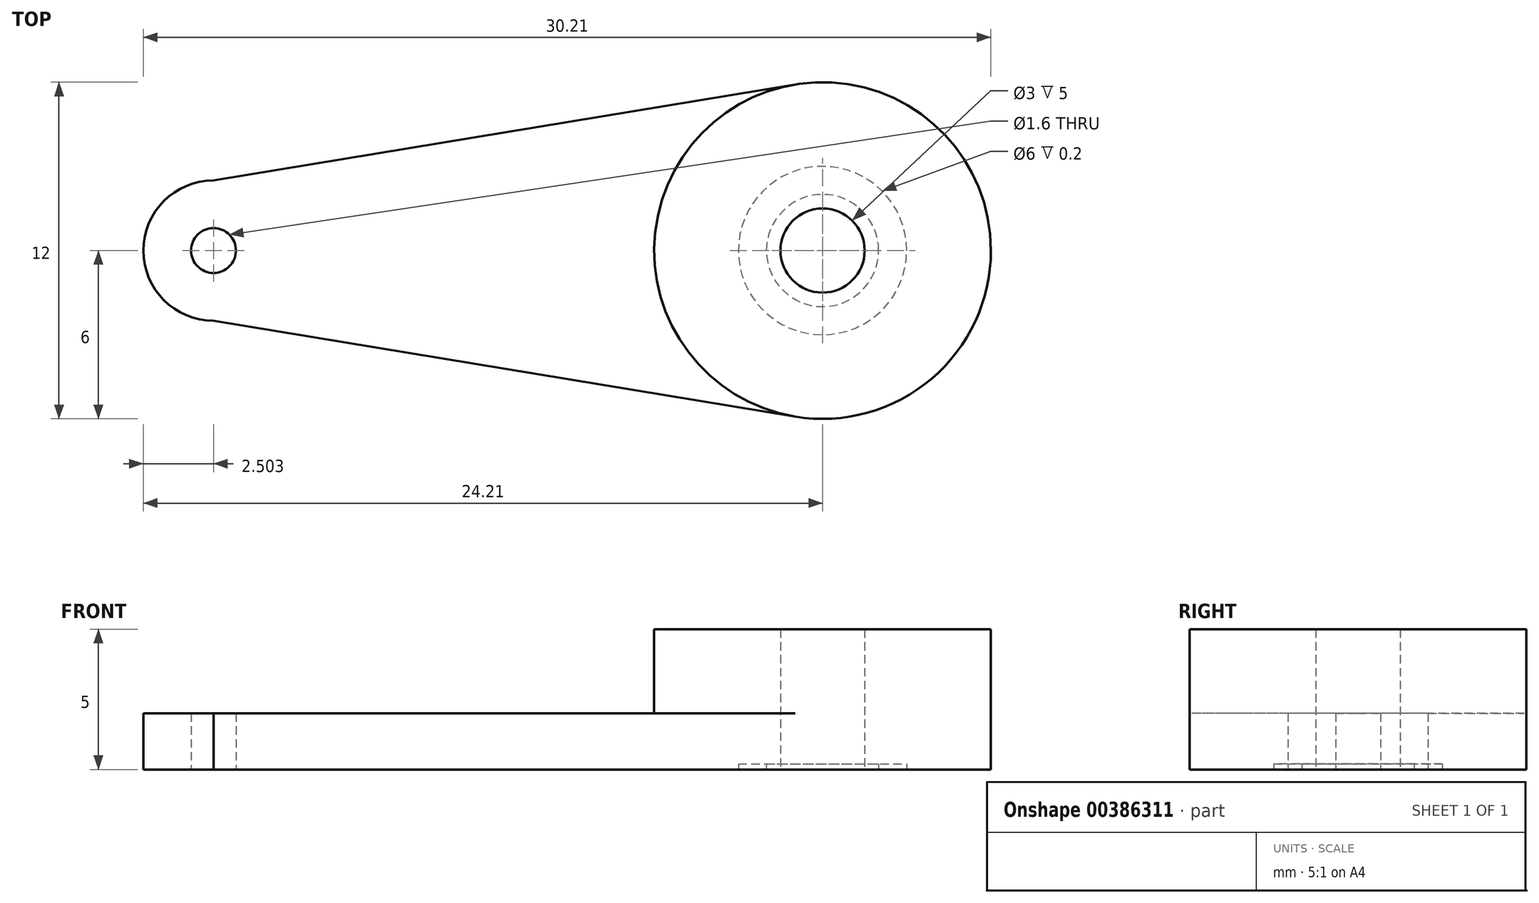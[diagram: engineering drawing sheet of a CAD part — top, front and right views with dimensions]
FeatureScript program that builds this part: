
annotation { "Feature Type Name" : "Feature", "Feature Type Description" : "" }
export const myFeature = defineFeature(function(context is Context, id is Id, definition is map)
    precondition{}
    {
        {
            var Q0;
            Q0=qCreatedBy(makeId("Top.planeOp"),FACE);
            var sketch = newSketch(context, id + "F0", { "sketchPlane" : qUnion([Q0]), "disableImprinting" : false});
            skCircle(sketch, "E0", {"center": v(0, 0) * mm, "radius": 6 * mm});
            skCircle(sketch, "E1", {"center": v(-21.7, 0) * mm, "radius": 2.5 * mm});
            skLineSegment(sketch, "E2", {"start": v(-21.7, 2.5) * mm, "end": v(0, 6.08) * mm});
            skLineSegment(sketch, "E3", {"start": v(-21.7, -2.5) * mm, "end": v(0, -6.08) * mm});
            skCircle(sketch, "E4", {"center": v(0, 0) * mm, "radius": 1.5 * mm});
            skCircle(sketch, "E5", {"center": v(-21.7, 0) * mm, "radius": 0.8 * mm});
            skSolve(sketch);
        }
        {
            var Q0;
            Q0=makeQuery(id+"F0.imprint","IMPRINT",FACE,{"disambiguationData":[TD([[makeQuery(id+"F0.imprint","IMPRINT",EDGE,{"derivedFrom":sQuery(id+"F0.wireOp",EDGE,"E4")}),-1.0]])]});
            extrude(context, id + "F1", {"entities" : qUnion([Q0]), "depth" : 5 * mm});
        }
        {
            var Q0;
            {var subQ0=sQuery(id+"F0.wireOp",EDGE,"E2");var subQ1=sQuery(id+"F0.wireOp",EDGE,"E0");var subQ2=makeQuery(id+"F0.imprint","INTERSECT",VERTEX,{"derivedFrom":[subQ1,subQ0]});Q0=makeQuery(id+"F0.imprint","IMPRINT",FACE,{"disambiguationData":[TD([[makeQuery(id+"F0.imprint","IMPRINT",EDGE,{"disambiguationData":[TD([[subQ2,-1.0]])],"derivedFrom":subQ1}),-1.0]])]});}
            var Q1;
            Q1=makeQuery(id+"F0.imprint","IMPRINT",FACE,{"disambiguationData":[TD([[makeQuery(id+"F0.imprint","IMPRINT",EDGE,{"derivedFrom":sQuery(id+"F0.wireOp",EDGE,"E5")}),-1.0]])]});
            extrude(context, id + "F2", {"entities" : qUnion([Q0, Q1]), "operationType" : NewBodyOperationType.ADD, "depth" : 2 * mm});
        }
        {
            var Q0;
            {var subQ0=sQuery(id+"F0.wireOp",EDGE,"E0");Q0=makeQuery(id+"F2.boolean.opBoolean","MERGE",FACE,{"derivedFrom":[makeQuery(id+"F1.opExtrude","CAP_FACE",FACE,{"disambiguationData":[OSD([subQ0,sQuery(id+"F0.wireOp",EDGE,"E4")])],"isStart":true}),makeQuery(id+"F2.opExtrude","CAP_FACE",FACE,{"disambiguationData":[OSD([subQ0,sQuery(id+"F0.wireOp",EDGE,"E1"),sQuery(id+"F0.wireOp",EDGE,"E2"),sQuery(id+"F0.wireOp",EDGE,"E3"),sQuery(id+"F0.wireOp",EDGE,"E5")])],"isStart":true})]});}
            var sketch = newSketch(context, id + "F3", { "sketchPlane" : qUnion([Q0]), "disableImprinting" : false});
            skCircle(sketch, "E6", {"center": v(0, 0) * mm, "radius": 2 * mm});
            skCircle(sketch, "E7", {"center": v(0, 0) * mm, "radius": 3 * mm});
            skSolve(sketch);
        }
        {
            var Q0;
            Q0=qSketchRegion(id+"F3",true);
            extrude(context, id + "F4", {"entities" : qUnion([Q0]), "operationType" : NewBodyOperationType.REMOVE, "oppositeDirection" : true, "depth" : 0.2 * mm});
        }
    });
